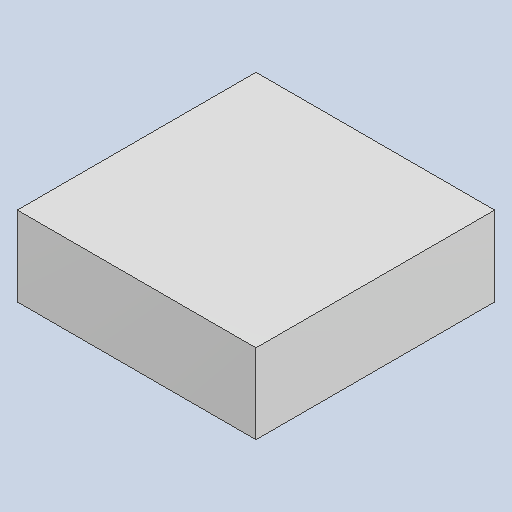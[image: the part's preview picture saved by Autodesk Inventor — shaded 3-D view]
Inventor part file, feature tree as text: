
AUTODESK INVENTOR PART (.ipt)
format: ipt  version: 2023.4 (Build 274418000, 418)  size: 79,872 bytes
history: native  units: mm
features: extrude x1
ambient origin geometry x8: Origin, YZ Plane, XZ Plane, XY Plane, X Axis, Y Axis, Z Axis, Center Point
bodies: Solid1 (feature_tree)
feature tree (1):
  extrude  "Extruded_35"  [1 undecoded]
note: 1 required parameter value undecoded (feature->parameter linkage not recoverable at this tier; creation-order binding heuristic only, values carry confidence <= 0.55)
